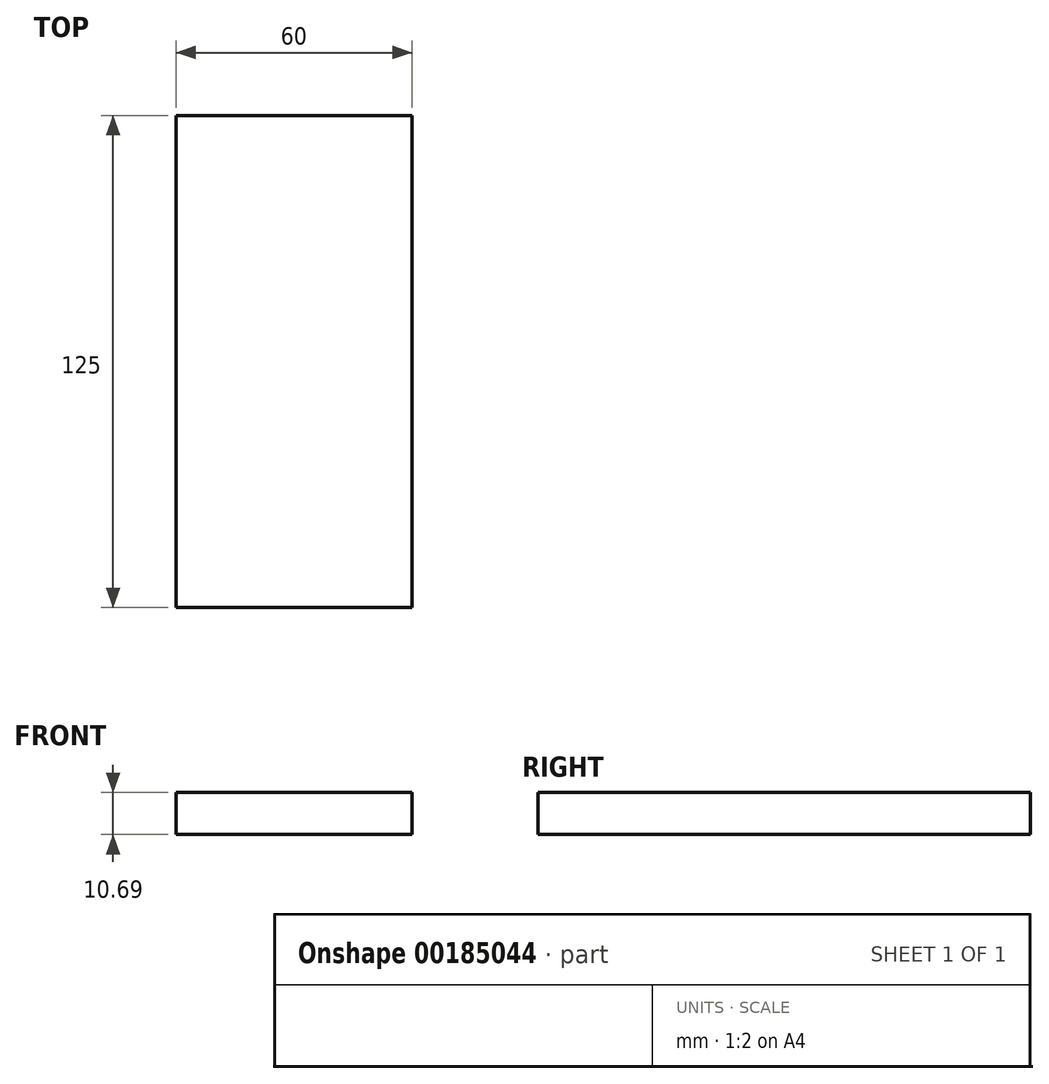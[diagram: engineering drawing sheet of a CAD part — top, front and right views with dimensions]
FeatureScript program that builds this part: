
annotation { "Feature Type Name" : "Feature", "Feature Type Description" : "" }
export const myFeature = defineFeature(function(context is Context, id is Id, definition is map)
    precondition{}
    {
        {
            var Q0;
            Q0=qCreatedBy(makeId("Top.planeOp"),FACE);
            var sketch = newSketch(context, id + "F0", { "sketchPlane" : qUnion([Q0])});
            skLineSegment(sketch, "E0.bottom", {"start": v(30, 62.5) * mm, "end": v(-30, 62.5) * mm});
            skLineSegment(sketch, "E0.top", {"start": v(30, -62.5) * mm, "end": v(-30, -62.5) * mm});
            skLineSegment(sketch, "E0.left", {"start": v(30, 62.5) * mm, "end": v(30, -62.5) * mm});
            skLineSegment(sketch, "E0.right", {"start": v(-30, 62.5) * mm, "end": v(-30, -62.5) * mm});
            skPoint(sketch, "E0.middle", {"position": v(0, 0) * mm});
            skSolve(sketch);
        }
        {
            var Q0;
            Q0 = qSketchRegion(id + "F0", true);
            extrude(context, id + "F1", {"entities" : qUnion([Q0]), "depth" : 10.7 * mm});
        }
    });
